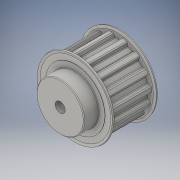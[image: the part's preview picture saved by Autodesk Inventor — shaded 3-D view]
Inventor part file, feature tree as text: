
AUTODESK INVENTOR PART (.ipt)
format: ipt  version: 2016 (Build 200138000, 138)  size: 369,664 bytes
history: native  units: in
note: dims shown in document units (in); Inventor stores cm internally (conversion verified against a paired STEP export)
features: chamfer x2, extrude x1, sketch x1, imported_body x1
ambient origin geometry x8: Origin, YZ Plane, XZ Plane, XY Plane, X Axis, Y Axis, Z Axis, Center Point
bodies: Solid1 (feature_tree)
feature tree (5):
  extrude  "Extrusion1"  Depth=1.5748in TaperAngle=0.0deg
  chamfer  "Chamfer1"  Distance=0.0098in Angle=45.0deg
  chamfer  "Chamfer2"  Distance=0.0098in Angle=45.0deg
  sketch  "Sketch1"  dims[d0=0.251in d1=1.5748in d2=0.0in d3=0.0098in d4=0.0787in d5=45.0deg d6=0.0098in d7=0.0787in d8=45.0deg]
  imported_body  "Base1"
